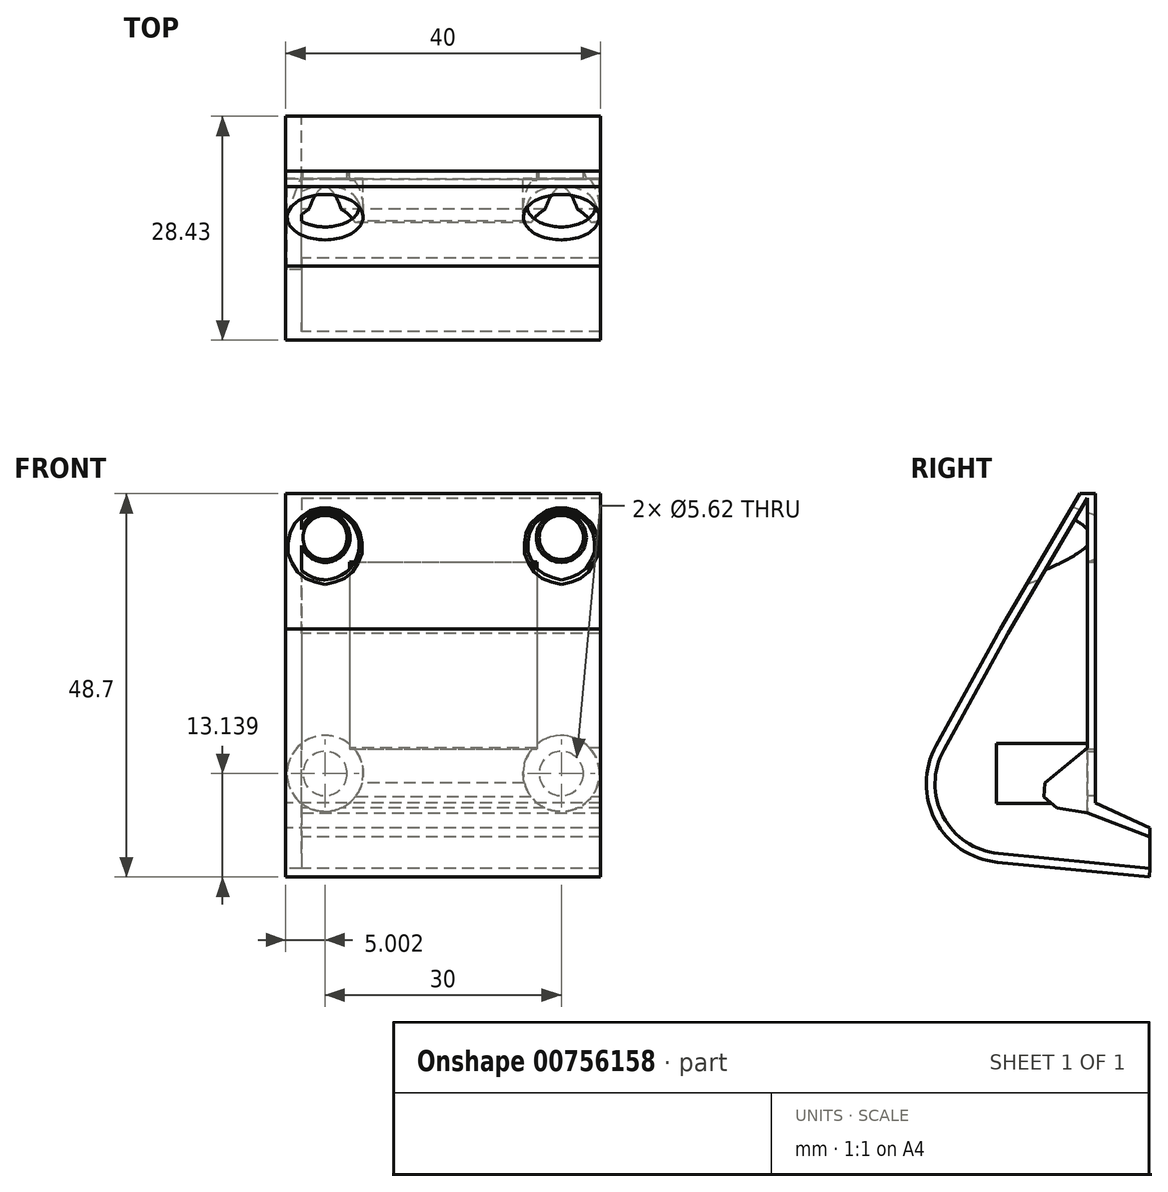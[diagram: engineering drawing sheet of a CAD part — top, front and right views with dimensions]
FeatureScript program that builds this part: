
annotation { "Feature Type Name" : "Feature", "Feature Type Description" : "" }
export const myFeature = defineFeature(function(context is Context, id is Id, definition is map)
    precondition{}
    {
        {
            var Q0;
            Q0=qCreatedBy(makeId("Front.planeOp"),FACE);
            var sketch = newSketch(context, id + "F0", { "sketchPlane" : qUnion([Q0])});
            skLineSegment(sketch, "E0.bottom", {"start": v(-13.53, 11.93) * mm, "end": v(26.47, 11.93) * mm});
            skLineSegment(sketch, "E0.top", {"start": v(-13.53, -28.07) * mm, "end": v(26.47, -28.07) * mm});
            skLineSegment(sketch, "E0.left", {"start": v(-13.53, 11.93) * mm, "end": v(-13.53, -28.07) * mm});
            skLineSegment(sketch, "E0.right", {"start": v(26.47, 11.93) * mm, "end": v(26.47, -28.07) * mm});
            skCircle(sketch, "E1", {"center": v(21.47, 6.93) * mm, "radius": 2.8 * mm});
            skCircle(sketch, "E2", {"center": v(-8.53, 6.93) * mm, "radius": 2.8 * mm});
            skCircle(sketch, "E3", {"center": v(-8.53, -23.07) * mm, "radius": 2.8 * mm});
            skCircle(sketch, "E4", {"center": v(21.47, -23.07) * mm, "radius": 2.8 * mm});
            skLineSegment(sketch, "E5.0", {"start": v(-5.43, 3.83) * mm, "end": v(18.37, 3.83) * mm});
            skLineSegment(sketch, "E5.1", {"start": v(-5.43, 3.83) * mm, "end": v(-5.43, -19.97) * mm});
            skLineSegment(sketch, "E5.2", {"start": v(-5.43, -19.97) * mm, "end": v(18.37, -19.97) * mm});
            skLineSegment(sketch, "E5.3", {"start": v(18.37, 3.83) * mm, "end": v(18.37, -19.97) * mm});
            skCircle(sketch, "E6.0", {"center": v(21.47, -23.07) * mm, "radius": 4.84 * mm});
            skCircle(sketch, "E7.0", {"center": v(-8.53, -23.07) * mm, "radius": 4.84 * mm});
            skSolve(sketch);
        }
        {
            var Q0;
            Q0=makeQuery(id+"F0.imprint","IMPRINT",FACE,{"disambiguationData":[TD([[makeQuery(id+"F0.imprint","IMPRINT",EDGE,{"derivedFrom":sQuery(id+"F0.wireOp",EDGE,"E0.bottom")}),-1.0]])]});
            var Q1;
            Q1=makeQuery(id+"F0.imprint","IMPRINT",FACE,{"disambiguationData":[TD([[makeQuery(id+"F0.imprint","IMPRINT",EDGE,{"derivedFrom":sQuery(id+"F0.wireOp",EDGE,"E3")}),-1.0]])]});
            var Q2;
            Q2=makeQuery(id+"F0.imprint","IMPRINT",FACE,{"disambiguationData":[TD([[makeQuery(id+"F0.imprint","IMPRINT",EDGE,{"derivedFrom":sQuery(id+"F0.wireOp",EDGE,"E4")}),-1.0]])]});
            extrude(context, id + "F1", {"entities" : qUnion([Q0, Q1, Q2]), "depth" : 1 * mm, "offsetDistance" : 25.4 * mm});
        }
        {
            var Q0;
            Q0=makeQuery(id+"F1.opExtrude","SWEPT_FACE",FACE,{"disambiguationData":[OSD([sQuery(id+"F0.wireOp",EDGE,"E0.left")])]});
            var sketch = newSketch(context, id + "F2", { "sketchPlane" : qUnion([Q0])});
            skLineSegment(sketch, "E8", {"start": v(1, -28.07) * mm, "end": v(-6.97, -31.11) * mm});
            skLineSegment(sketch, "E9", {"start": v(-6.97, -31.11) * mm, "end": v(-6.97, -35.1) * mm});
            skLineSegment(sketch, "E10", {"start": v(11.06, -5.26) * mm, "end": v(1, 11.93) * mm});
            skLineSegment(sketch, "E11", {"start": v(11.06, -5.26) * mm, "end": v(19.23, -20.08) * mm});
            skLineSegment(sketch, "E12", {"start": v(12.31, -33.22) * mm, "end": v(-6.97, -35.1) * mm});
            skLineSegment(sketch, "E13", {"start": v(1, -19.85) * mm, "end": v(6.36, -24.25) * mm});
            skLineSegment(sketch, "E14", {"start": v(6.36, -24.25) * mm, "end": v(6.54, -26.03) * mm});
            skLineSegment(sketch, "E15", {"start": v(6.54, -26.03) * mm, "end": v(4.83, -27.46) * mm});
            skLineSegment(sketch, "E16", {"start": v(4.83, -27.46) * mm, "end": v(1, -28.07) * mm});
            skArc(sketch, "E17", {"start": v(12.31, -33.22) * mm, "mid": v(19.32, -28.52) * mm, "end": v(19.23, -20.08) * mm});
            skLineSegment(sketch, "E18.0", {"start": v(12.03, -4.71) * mm, "end": v(1.96, 12.5) * mm});
            skLineSegment(sketch, "E18.1", {"start": v(12.03, -4.71) * mm, "end": v(20.21, -19.54) * mm});
            skArc(sketch, "E18.2", {"start": v(12.42, -34.33) * mm, "mid": v(20.3, -29.04) * mm, "end": v(20.21, -19.54) * mm});
            skLineSegment(sketch, "E18.3", {"start": v(12.42, -34.33) * mm, "end": v(-6.86, -36.21) * mm});
            skLineSegment(sketch, "E19", {"start": v(1.96, 12.5) * mm, "end": v(0, 12.5) * mm});
            skLineSegment(sketch, "E20", {"start": v(0, 12.5) * mm, "end": v(0, 11.93) * mm});
            skLineSegment(sketch, "E21", {"start": v(-6.97, -35.1) * mm, "end": v(-6.86, -36.21) * mm});
            skLineSegment(sketch, "E22", {"start": v(-6.97, -31.11) * mm, "end": v(-6.97, -30) * mm});
            skLineSegment(sketch, "E23", {"start": v(-6.97, -30) * mm, "end": v(0, -26.78) * mm});
            skSolve(sketch);
        }
        {
            var Q0;
            Q0=makeQuery(id+"F2.imprint","IMPRINT",FACE,{"disambiguationData":[TD([[makeQuery(id+"F2.imprint","IMPRINT",EDGE,{"derivedFrom":sQuery(id+"F2.wireOp",EDGE,"E10")}),-1.0]])]});
            var Q1;
            {var subQ1=sQuery(id+"F2.wireOp",EDGE,"E13");Q1=makeQuery(id+"F2.imprint","IMPRINT",FACE,{"disambiguationData":[TD([[makeQuery(id+"F2.imprint","IMPRINT",EDGE,{"derivedFrom":subQ1}),-1.0]])]});}
            var Q2;
            Q2=makeQuery(id+"F2.imprint","IMPRINT",FACE,{"disambiguationData":[TD([[makeQuery(id+"F2.imprint","IMPRINT",EDGE,{"derivedFrom":sQuery(id+"F2.wireOp",EDGE,"E8")}),-1.0]])]});
            extrude(context, id + "F3", {"entities" : qUnion([Q0, Q1, Q2]), "operationType" : NewBodyOperationType.ADD, "oppositeDirection" : true, "depth" : 40 * mm, "offsetDistance" : 25.4 * mm});
        }
        {
            var Q0;
            Q0=makeQuery(id+"F2.imprint","IMPRINT",FACE,{"disambiguationData":[TD([[makeQuery(id+"F2.imprint","IMPRINT",EDGE,{"derivedFrom":sQuery(id+"F2.wireOp",EDGE,"E8")}),1.0]])]});
            extrude(context, id + "F4", {"entities" : qUnion([Q0]), "operationType" : NewBodyOperationType.ADD, "oppositeDirection" : true, "depth" : 2 * mm, "offsetDistance" : 25.4 * mm});
        }
        {
            var Q0;
            Q0=makeQuery(id+"F0.imprint","IMPRINT",FACE,{"disambiguationData":[TD([[makeQuery(id+"F0.imprint","IMPRINT",EDGE,{"derivedFrom":sQuery(id+"F0.wireOp",EDGE,"E1")}),1.0]])]});
            extrude(context, id + "F5", {"entities" : qUnion([Q0]), "operationType" : NewBodyOperationType.REMOVE, "depth" : 18.29 * mm, "offsetDistance" : 25.4 * mm, "hasDraft" : true, "draftAngle" : 20 * degree});
        }
        {
            var Q0;
            Q0=makeQuery(id+"F0.imprint","IMPRINT",FACE,{"disambiguationData":[TD([[makeQuery(id+"F0.imprint","IMPRINT",EDGE,{"derivedFrom":sQuery(id+"F0.wireOp",EDGE,"E2")}),1.0]])]});
            extrude(context, id + "F6", {"entities" : qUnion([Q0]), "operationType" : NewBodyOperationType.REMOVE, "depth" : 9.07 * mm, "offsetDistance" : 25.4 * mm, "hasDraft" : true, "draftAngle" : 20 * degree});
        }
        {
            var Q0;
            Q0=makeQuery(id+"F0.imprint","IMPRINT",FACE,{"disambiguationData":[TD([[makeQuery(id+"F0.imprint","IMPRINT",EDGE,{"derivedFrom":sQuery(id+"F0.wireOp",EDGE,"E4")}),-1.0]])]});
            var Q1;
            Q1=makeQuery(id+"F0.imprint","IMPRINT",FACE,{"disambiguationData":[TD([[makeQuery(id+"F0.imprint","IMPRINT",EDGE,{"derivedFrom":sQuery(id+"F0.wireOp",EDGE,"E3")}),-1.0]])]});
            var Q2;
            Q2=makeQuery(id+"F0.imprint","IMPRINT",FACE,{"disambiguationData":[TD([[makeQuery(id+"F0.imprint","IMPRINT",EDGE,{"derivedFrom":sQuery(id+"F0.wireOp",EDGE,"E4")}),1.0]])]});
            var Q3;
            Q3=makeQuery(id+"F0.imprint","IMPRINT",FACE,{"disambiguationData":[TD([[makeQuery(id+"F0.imprint","IMPRINT",EDGE,{"derivedFrom":sQuery(id+"F0.wireOp",EDGE,"E3")}),1.0]])]});
            extrude(context, id + "F7", {"entities" : qUnion([Q0, Q1, Q2, Q3]), "operationType" : NewBodyOperationType.REMOVE, "depth" : 12.52 * mm, "offsetDistance" : 25.4 * mm, "hasSecondDirection" : true, "secondDirectionOppositeDirection" : false, "secondDirectionDepth" : 0.97 * mm});
        }
    });
